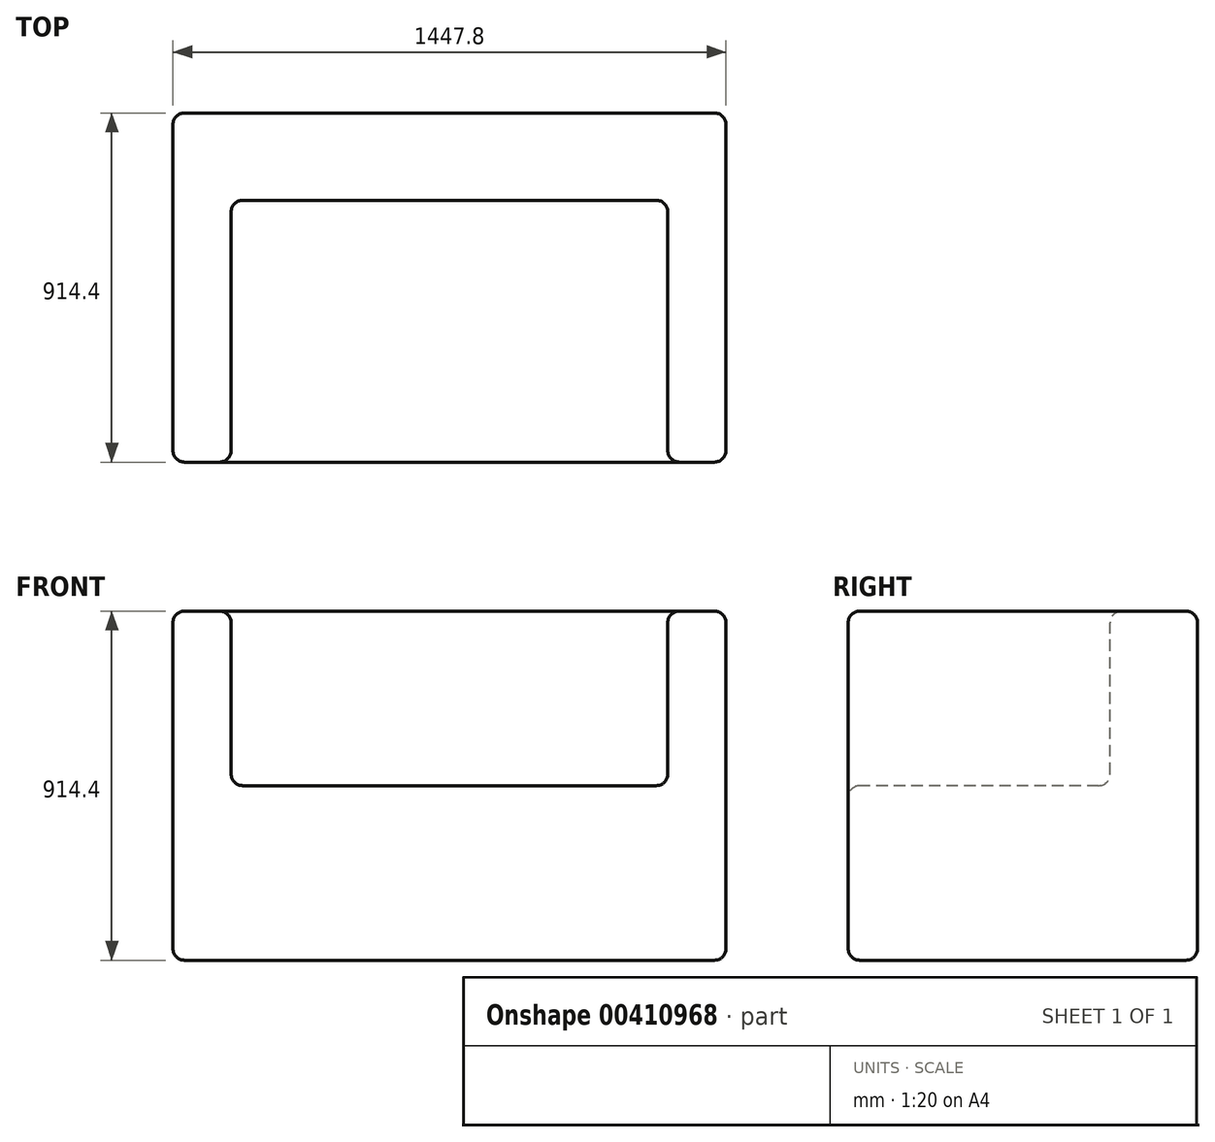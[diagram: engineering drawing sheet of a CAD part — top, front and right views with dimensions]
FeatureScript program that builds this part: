
annotation { "Feature Type Name" : "Feature", "Feature Type Description" : "" }
export const myFeature = defineFeature(function(context is Context, id is Id, definition is map)
    precondition{}
    {
        {
            var Q0;
            Q0=qCreatedBy(makeId("Top.planeOp"),FACE);
            var sketch = newSketch(context, id + "F0", { "sketchPlane" : qUnion([Q0])});
            skLineSegment(sketch, "E0.bottom", {"start": v(723.9, -457.2) * mm, "end": v(-723.9, -457.2) * mm});
            skLineSegment(sketch, "E0.top", {"start": v(723.9, 457.2) * mm, "end": v(-723.9, 457.2) * mm});
            skLineSegment(sketch, "E0.left", {"start": v(723.9, -457.2) * mm, "end": v(723.9, 457.2) * mm});
            skLineSegment(sketch, "E0.right", {"start": v(-723.9, -457.2) * mm, "end": v(-723.9, 457.2) * mm});
            skPoint(sketch, "E0.middle", {"position": v(0, 0) * mm});
            skSolve(sketch);
        }
        {
            var Q0;
            Q0=makeQuery(id+"F0.imprint","IMPRINT",FACE,{"disambiguationData":[TD([[makeQuery(id+"F0.imprint","IMPRINT",EDGE,{"derivedFrom":sQuery(id+"F0.wireOp",EDGE,"E0.bottom")}),-1.0]])]});
            extrude(context, id + "F1", {"entities" : qUnion([Q0]), "depth" : 914.4 * mm});
        }
        {
            var Q0;
            Q0=makeQuery(id+"F1.opExtrude","CAP_FACE",FACE,{"disambiguationData":[OSD([sQuery(id+"F0.wireOp",EDGE,"E0.bottom"),sQuery(id+"F0.wireOp",EDGE,"E0.top"),sQuery(id+"F0.wireOp",EDGE,"E0.left"),sQuery(id+"F0.wireOp",EDGE,"E0.right")])],"isStart":false});
            var sketch = newSketch(context, id + "F2", { "sketchPlane" : qUnion([Q0])});
            skLineSegment(sketch, "E1", {"start": v(-571.5, -457.2) * mm, "end": v(-571.5, 228.6) * mm});
            skLineSegment(sketch, "E2", {"start": v(-571.5, 228.6) * mm, "end": v(571.5, 228.6) * mm});
            skLineSegment(sketch, "E3", {"start": v(571.5, 228.6) * mm, "end": v(571.5, -457.2) * mm});
            skSolve(sketch);
        }
        {
            var Q0;
            {var subQ0=sQuery(id+"F2.wireOp",EDGE,"E1");Q0=makeQuery(id+"F2.imprint","IMPRINT",FACE,{"disambiguationData":[TD([[makeQuery(id+"F2.imprint","IMPRINT",EDGE,{"derivedFrom":subQ0}),-1.0]])]});}
            extrude(context, id + "F3", {"entities" : qUnion([Q0]), "operationType" : NewBodyOperationType.REMOVE, "oppositeDirection" : true, "depth" : 457.2 * mm});
        }
        {
            var Q0;
            Q0=makeQuery(id+"F1.opExtrude","SWEPT_FACE",FACE,{"disambiguationData":[OSD([sQuery(id+"F0.wireOp",EDGE,"E0.bottom")])]});
            var Q1;
            Q1=makeQuery(id+"F1.opExtrude","SWEPT_FACE",FACE,{"disambiguationData":[OSD([sQuery(id+"F0.wireOp",EDGE,"E0.left")])]});
            var Q2;
            Q2=makeQuery(id+"F1.opExtrude","CAP_FACE",FACE,{"disambiguationData":[OSD([sQuery(id+"F0.wireOp",EDGE,"E0.bottom"),sQuery(id+"F0.wireOp",EDGE,"E0.top"),sQuery(id+"F0.wireOp",EDGE,"E0.left"),sQuery(id+"F0.wireOp",EDGE,"E0.right")])],"isStart":false});
            var Q3;
            Q3=makeQuery(id+"F3.boolean.opBoolean","COPY",FACE,{"derivedFrom":makeQuery(id+"F3.opExtrude","CAP_FACE",FACE,{"disambiguationData":[OSD([sQuery(id+"F0.wireOp",EDGE,"E0.bottom"),sQuery(id+"F2.wireOp",EDGE,"E1"),sQuery(id+"F2.wireOp",EDGE,"E2"),sQuery(id+"F2.wireOp",EDGE,"E3")])],"isStart":false})});
            var Q4;
            Q4=makeQuery(id+"F3.boolean.opBoolean","COPY",FACE,{"derivedFrom":makeQuery(id+"F3.opExtrude","SWEPT_FACE",FACE,{"disambiguationData":[OSD([sQuery(id+"F2.wireOp",EDGE,"E2")])]})});
            var Q5;
            Q5=makeQuery(id+"F3.boolean.opBoolean","COPY",FACE,{"derivedFrom":makeQuery(id+"F3.opExtrude","SWEPT_FACE",FACE,{"disambiguationData":[OSD([sQuery(id+"F2.wireOp",EDGE,"E1")])]})});
            var Q6;
            Q6=makeQuery(id+"F3.boolean.opBoolean","COPY",FACE,{"derivedFrom":makeQuery(id+"F3.opExtrude","SWEPT_FACE",FACE,{"disambiguationData":[OSD([sQuery(id+"F2.wireOp",EDGE,"E3")])]})});
            var Q7;
            Q7=makeQuery(id+"F1.opExtrude","SWEPT_FACE",FACE,{"disambiguationData":[OSD([sQuery(id+"F0.wireOp",EDGE,"E0.right")])]});
            var Q8;
            Q8=makeQuery(id+"F1.opExtrude","SWEPT_FACE",FACE,{"disambiguationData":[OSD([sQuery(id+"F0.wireOp",EDGE,"E0.top")])]});
            fillet(context, id + "F4", {"entities" : qUnion([Q0, Q1, Q2, Q3, Q4, Q5, Q6, Q7, Q8]), "radius" : 30.48 * mm, "tangentPropagation" : true, "allowEdgeOverflow" : false});
        }
    });
